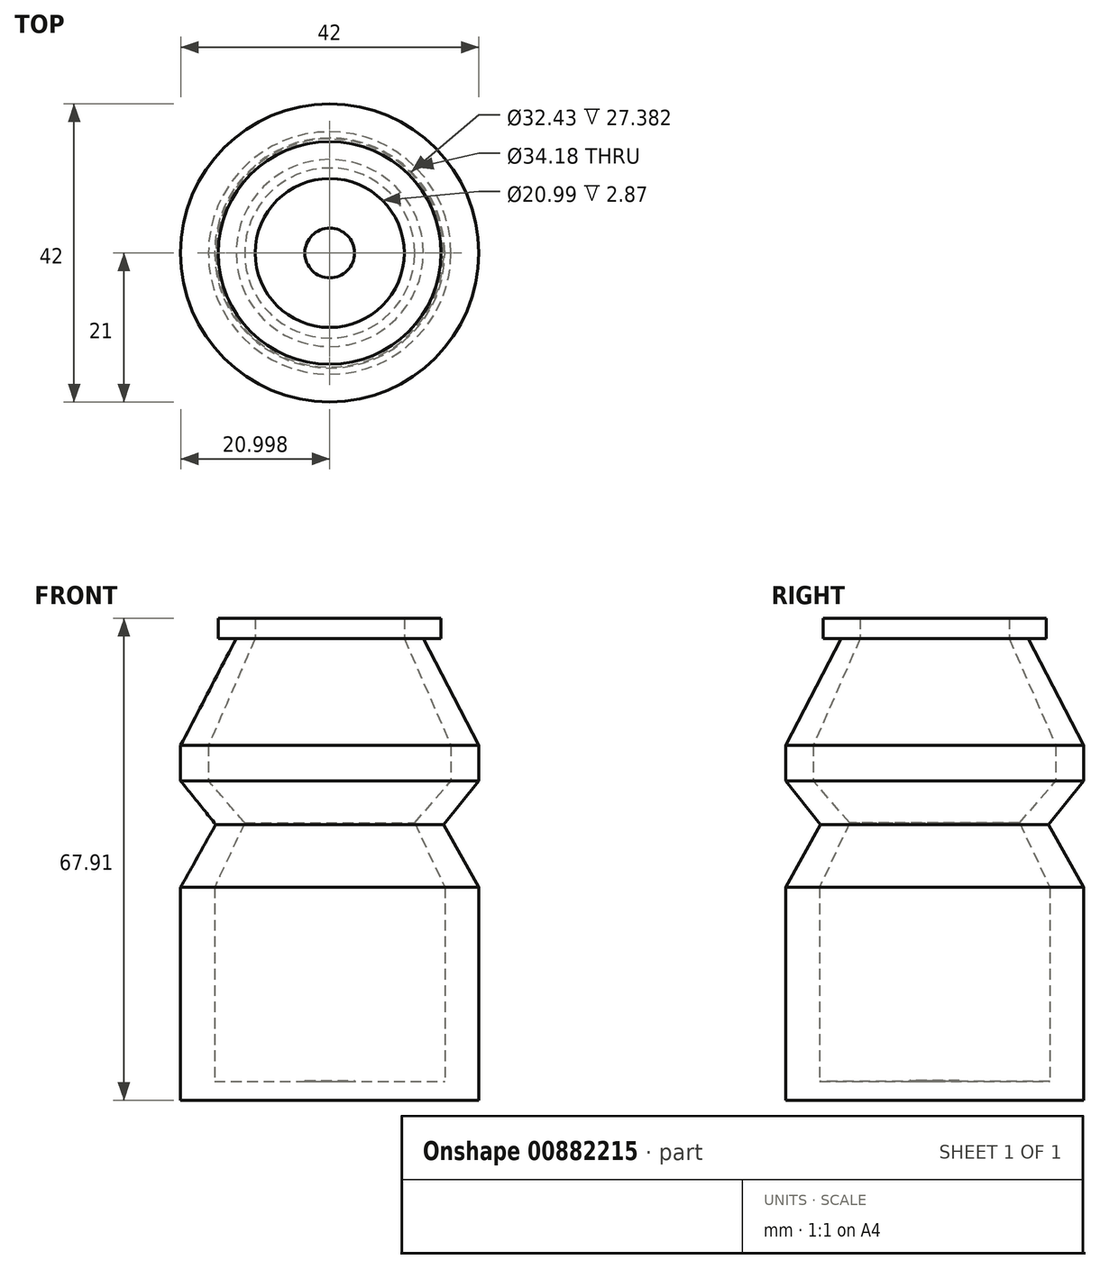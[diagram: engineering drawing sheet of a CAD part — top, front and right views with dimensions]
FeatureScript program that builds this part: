
annotation { "Feature Type Name" : "Feature", "Feature Type Description" : "" }
export const myFeature = defineFeature(function(context is Context, id is Id, definition is map)
    precondition{}
    {
        {
            var Q0;
            Q0=qCreatedBy(makeId("Front.planeOp"),FACE);
            var sketch = newSketch(context, id + "F0", { "sketchPlane" : qUnion([Q0])});
            skLineSegment(sketch, "E0", {"start": v(-2.24, -75) * mm, "end": v(-19.74, -75) * mm});
            skLineSegment(sketch, "E1", {"start": v(-19.74, -75) * mm, "end": v(-19.74, -45) * mm});
            skLineSegment(sketch, "E2", {"start": v(-19.74, -45) * mm, "end": v(-14.8, -36.15) * mm});
            skLineSegment(sketch, "E3", {"start": v(-14.8, -36.15) * mm, "end": v(-19.74, -30) * mm});
            skLineSegment(sketch, "E4", {"start": v(-19.74, -30) * mm, "end": v(-19.74, -25) * mm});
            skLineSegment(sketch, "E5", {"start": v(-14.96, -45) * mm, "end": v(-10.72, -35.92) * mm});
            skLineSegment(sketch, "E6", {"start": v(-10.72, -35.92) * mm, "end": v(-15.83, -30) * mm});
            skLineSegment(sketch, "E7", {"start": v(-15.83, -30) * mm, "end": v(-15.83, -25) * mm});
            skLineSegment(sketch, "E8", {"start": v(-2.24, -75) * mm, "end": v(-2.24, -72.38) * mm});
            skLineSegment(sketch, "E9", {"start": v(-2.24, -72.38) * mm, "end": v(-14.96, -72.38) * mm});
            skLineSegment(sketch, "E10", {"start": v(-14.96, -45) * mm, "end": v(-14.96, -72.38) * mm});
            skLineSegment(sketch, "E11", {"start": v(-19.74, -25) * mm, "end": v(-11.93, -9.96) * mm});
            skLineSegment(sketch, "E12", {"start": v(-15.83, -25) * mm, "end": v(-9.24, -9.96) * mm});
            skLineSegment(sketch, "E13", {"start": v(-11.93, -9.96) * mm, "end": v(-14.44, -9.96) * mm});
            skLineSegment(sketch, "E14", {"start": v(-14.44, -9.96) * mm, "end": v(-14.44, -7.09) * mm});
            skLineSegment(sketch, "E15", {"start": v(-14.44, -7.09) * mm, "end": v(-9.24, -7.09) * mm});
            skLineSegment(sketch, "E16", {"start": v(-9.24, -7.09) * mm, "end": v(-9.24, -9.96) * mm});
            skLineSegment(sketch, "E17.bottom", {"start": v(-2.24, -75) * mm, "end": v(1.26, -75) * mm});
            skLineSegment(sketch, "E17.top", {"start": v(-2.24, -72.2) * mm, "end": v(1.26, -72.2) * mm});
            skLineSegment(sketch, "E17.left", {"start": v(-2.24, -75) * mm, "end": v(-2.24, -72.2) * mm});
            skLineSegment(sketch, "E17.right", {"start": v(1.26, -75) * mm, "end": v(1.26, -72.2) * mm});
            skSolve(sketch);
        }
        {
            var Q0;
            Q0 = qSketchRegion(id + "F0", true);
            var Q1;
            Q1=sQuery(id+"F0.wireOp",EDGE,"E17.right");
            revolve(context, id + "F1", {"surfaceOperationType" : NewSurfaceOperationType.NEW, "entities" : qUnion([Q0]), "axis" : qUnion([Q1]), "revolveType" : RevolveType.FULL});
        }
    });
